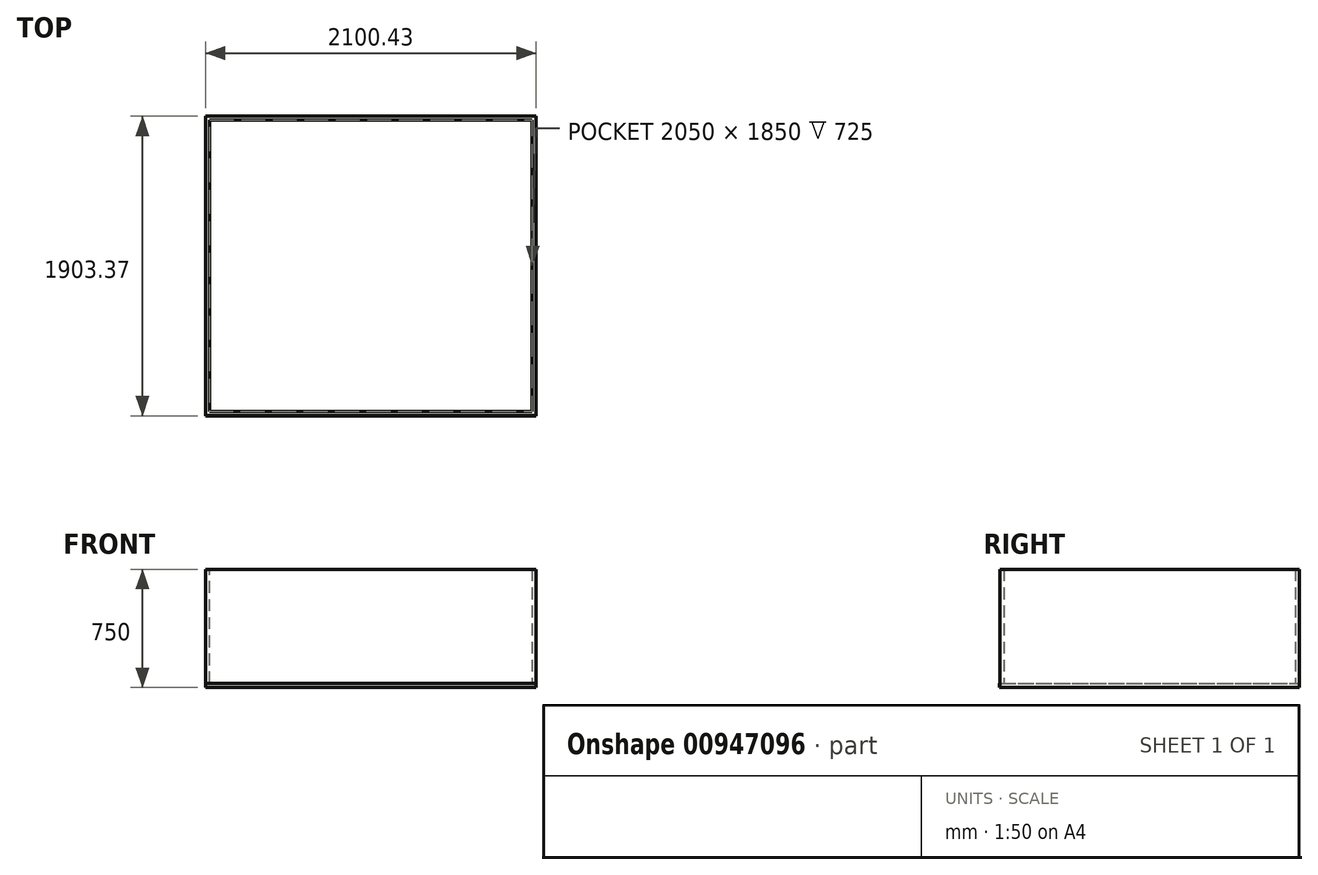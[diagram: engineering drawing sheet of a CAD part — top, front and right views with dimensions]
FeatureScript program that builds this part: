
annotation { "Feature Type Name" : "Feature", "Feature Type Description" : "" }
export const myFeature = defineFeature(function(context is Context, id is Id, definition is map)
    precondition{}
    {
        {
            var Q0;
            Q0=qCreatedBy(makeId("Top.planeOp"),FACE);
            var sketch = newSketch(context, id + "F0", { "sketchPlane" : qUnion([Q0])});
            skLineSegment(sketch, "E0.bottom", {"start": v(-1049.74, 832.38) * mm, "end": v(1050.26, 832.38) * mm});
            skLineSegment(sketch, "E0.top", {"start": v(-1049.74, -1067.62) * mm, "end": v(1050.26, -1067.62) * mm});
            skLineSegment(sketch, "E0.left", {"start": v(-1049.74, 832.38) * mm, "end": v(-1049.74, -1067.62) * mm});
            skLineSegment(sketch, "E0.right", {"start": v(1050.26, 832.38) * mm, "end": v(1050.26, -1067.62) * mm});
            skSolve(sketch);
        }
        {
            var Q0;
            Q0=sQuery(id+"F0.wireOp",EDGE,"E0.bottom");
            var Q1;
            Q1=sQuery(id+"F0.wireOp",EDGE,"E0.right");
            var Q2;
            Q2=sQuery(id+"F0.wireOp",EDGE,"E0.left");
            var Q3;
            Q3=sQuery(id+"F0.wireOp",EDGE,"E0.top");
            extrude(context, id + "F1", {"bodyType" : ToolBodyType.SURFACE, "surfaceEntities" : qUnion([Q0, Q1, Q2, Q3]), "depth" : 750 * mm, "offsetDistance" : 25 * mm});
        }
        {
            var Q0;
            Q0=makeQuery(id+"F1.opExtrude","SWEPT_FACE",FACE,{"disambiguationData":[OSD([sQuery(id+"F0.wireOp",EDGE,"E0.bottom")])]});
            extrude(context, id + "F2", {"entities" : qUnion([Q0]), "depth" : 25 * mm, "offsetDistance" : 25 * mm});
        }
        {
            var Q0;
            Q0=makeQuery(id+"F1.opExtrude","SWEPT_FACE",FACE,{"disambiguationData":[OSD([sQuery(id+"F0.wireOp",EDGE,"E0.right")])]});
            extrude(context, id + "F3", {"entities" : qUnion([Q0]), "operationType" : NewBodyOperationType.ADD, "depth" : 25 * mm, "offsetDistance" : 25 * mm});
        }
        {
            var Q0;
            Q0=makeQuery(id+"F1.opExtrude","SWEPT_FACE",FACE,{"disambiguationData":[OSD([sQuery(id+"F0.wireOp",EDGE,"E0.top")])]});
            extrude(context, id + "F4", {"entities" : qUnion([Q0]), "operationType" : NewBodyOperationType.ADD, "depth" : 25 * mm, "offsetDistance" : 25 * mm});
        }
        {
            var Q0;
            Q0=makeQuery(id+"F1.opExtrude","SWEPT_FACE",FACE,{"disambiguationData":[OSD([sQuery(id+"F0.wireOp",EDGE,"E0.left")])]});
            extrude(context, id + "F5", {"entities" : qUnion([Q0]), "operationType" : NewBodyOperationType.ADD, "depth" : 25 * mm, "offsetDistance" : 25 * mm});
        }
        {
            var Q0;
            Q0=qCreatedBy(makeId("Top.planeOp"),FACE);
            var sketch = newSketch(context, id + "F6", { "sketchPlane" : qUnion([Q0])});
            skLineSegment(sketch, "E1.bottom", {"start": v(-1050.17, -1071) * mm, "end": v(1049.83, -1071) * mm});
            skLineSegment(sketch, "E1.top", {"start": v(-1050.17, 829) * mm, "end": v(1049.83, 829) * mm});
            skLineSegment(sketch, "E1.left", {"start": v(-1050.17, -1071) * mm, "end": v(-1050.17, 829) * mm});
            skLineSegment(sketch, "E1.right", {"start": v(1049.83, -1071) * mm, "end": v(1049.83, 829) * mm});
            skSolve(sketch);
        }
        {
            var Q0;
            Q0 = qSketchRegion(id + "F6", true);
            extrude(context, id + "F7", {"entities" : qUnion([Q0]), "operationType" : NewBodyOperationType.ADD, "depth" : 25 * mm, "offsetDistance" : 25 * mm});
        }
        {
            var Q0;
            Q0=makeQuery(id+"F1.opExtrude","SWEPT_EDGE",EDGE,{"disambiguationData":[OSD([sQuery(id+"F0.wireOp",VERTEX,"E0.top.start")])]});
            var Q1;
            Q1=makeQuery(id+"F1.opExtrude","SWEPT_EDGE",EDGE,{"disambiguationData":[OSD([sQuery(id+"F0.wireOp",VERTEX,"E0.top.end")])]});
            var Q2;
            Q2=makeQuery(id+"F1.opExtrude","SWEPT_EDGE",EDGE,{"disambiguationData":[OSD([sQuery(id+"F0.wireOp",VERTEX,"E0.right.start")])]});
            var Q3;
            Q3=makeQuery(id+"F1.opExtrude","SWEPT_EDGE",EDGE,{"disambiguationData":[OSD([sQuery(id+"F0.wireOp",VERTEX,"E0.left.start")])]});
            fillet(context, id + "F8", {"entities" : qUnion([Q0, Q1, Q2, Q3]), "radius" : 20 * mm, "tangentPropagation" : true, "allowEdgeOverflow" : false});
        }
    });
